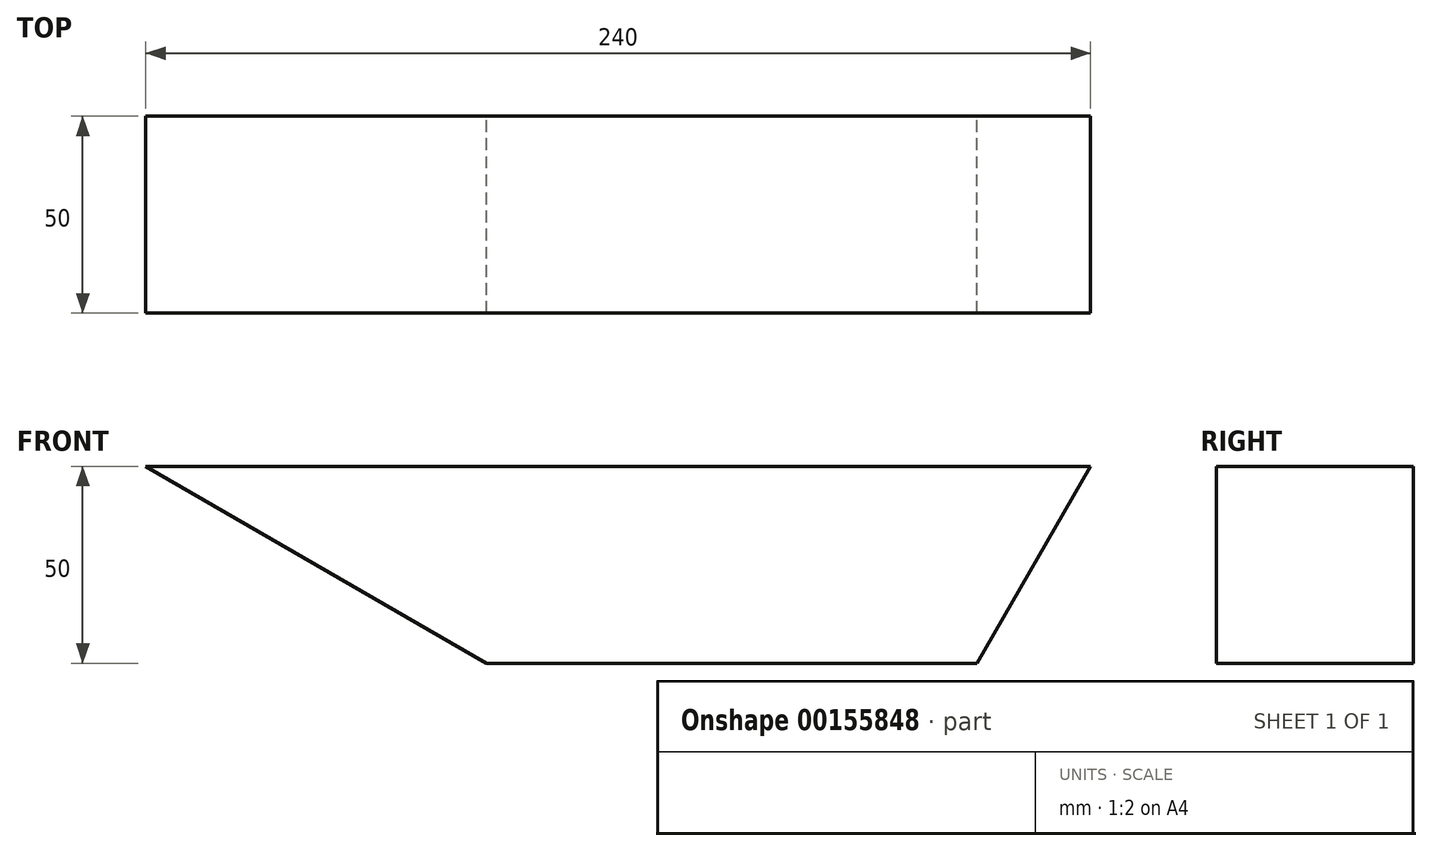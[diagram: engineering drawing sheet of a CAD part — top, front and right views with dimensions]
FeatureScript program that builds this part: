
annotation { "Feature Type Name" : "Feature", "Feature Type Description" : "" }
export const myFeature = defineFeature(function(context is Context, id is Id, definition is map)
    precondition{}
    {
        {
            var Q0;
            Q0=qCreatedBy(makeId("Front.planeOp"),FACE);
            var sketch = newSketch(context, id + "F0", { "sketchPlane" : qUnion([Q0])});
            skLineSegment(sketch, "E0", {"start": v(0, 0) * mm, "end": v(240, 0) * mm});
            skLineSegment(sketch, "E1", {"start": v(240, 0) * mm, "end": v(211.13, -50) * mm});
            skLineSegment(sketch, "E2", {"start": v(211.13, -50) * mm, "end": v(86.6, -50) * mm});
            skLineSegment(sketch, "E3", {"start": v(86.6, -50) * mm, "end": v(0, 0) * mm});
            skSolve(sketch);
        }
        {
            var Q0;
            Q0 = qSketchRegion(id + "F0", true);
            extrude(context, id + "F1", {"entities" : qUnion([Q0]), "depth" : 50 * mm});
        }
    });
